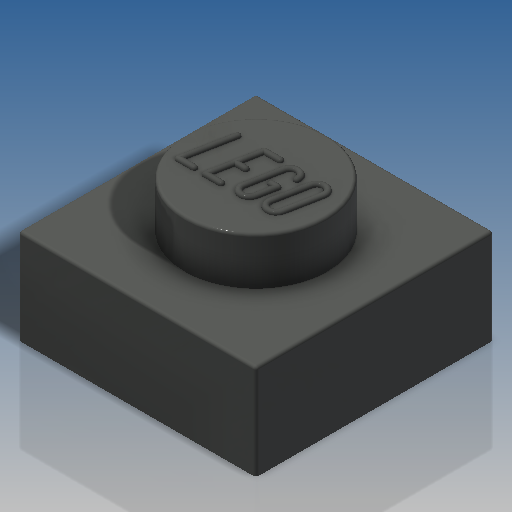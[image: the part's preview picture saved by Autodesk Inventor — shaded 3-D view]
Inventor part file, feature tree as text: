
AUTODESK INVENTOR PART (.ipt)
format: ipt  version: 2019.4 (Build 234330000, 330)  size: 6,198,784 bytes
history: native  units: in
note: dims shown in document units (in); Inventor stores cm internally (conversion verified against a paired STEP export)
features: sketch x4, extrude x3, fillet x2, other x1, pattern_linear x1
ambient origin geometry x8: Origin, YZ Plane, XZ Plane, XY Plane, X Axis, Y Axis, Z Axis, Center Point
bodies: Solid1 (feature_tree)
feature tree (11):
  extrude  "Extrusion1"  Depth=0.315in
  extrude  "Extrusion4"  Depth=0.063in
  other  "LEGO:1"
  fillet  "Fillet2"  Radius=0.063in
  pattern_linear  "Rectangular Pattern1"  Spacing1=0.189in  [1 undecoded]
  extrude  "Extrusion2"  Depth=0.315in
  fillet  "Fillet1"  Radius=0.1575in
  sketch  "Sketch2"  dims[d0=0.315in d1=0.315in]
  sketch  "Sketch3"  dims[d4=0.126in d5=0.0in d7=0.0591in d8=0.063in d11=0.063in d12=0.0in]
  sketch  "Sketch9"  dims[d22=0.0039in]
  sketch  "Sketch10"  dims[d62=0.063in d63=0.189in d64=0.1575in d65=0.1575in d66=0.063in d67=0.0in d68=0.0039in d69=0.3937in d71=0.315in d72=0.3937in d74=0.315in d86=0.0in d88=0.0in d89=0.0in d90=0.0in d91=0.0079in d92=0.0732in d93=0.0281in d94=0.035in d95=0.0079in d96=0.0139in d97=0.0281in d98=0.035in d99=0.0281in d100=0.0159in d101=0.0177in d102=0.035in d103=0.5428in]
note: 1 required parameter value undecoded (feature->parameter linkage not recoverable at this tier; creation-order binding heuristic only, values carry confidence <= 0.55)
